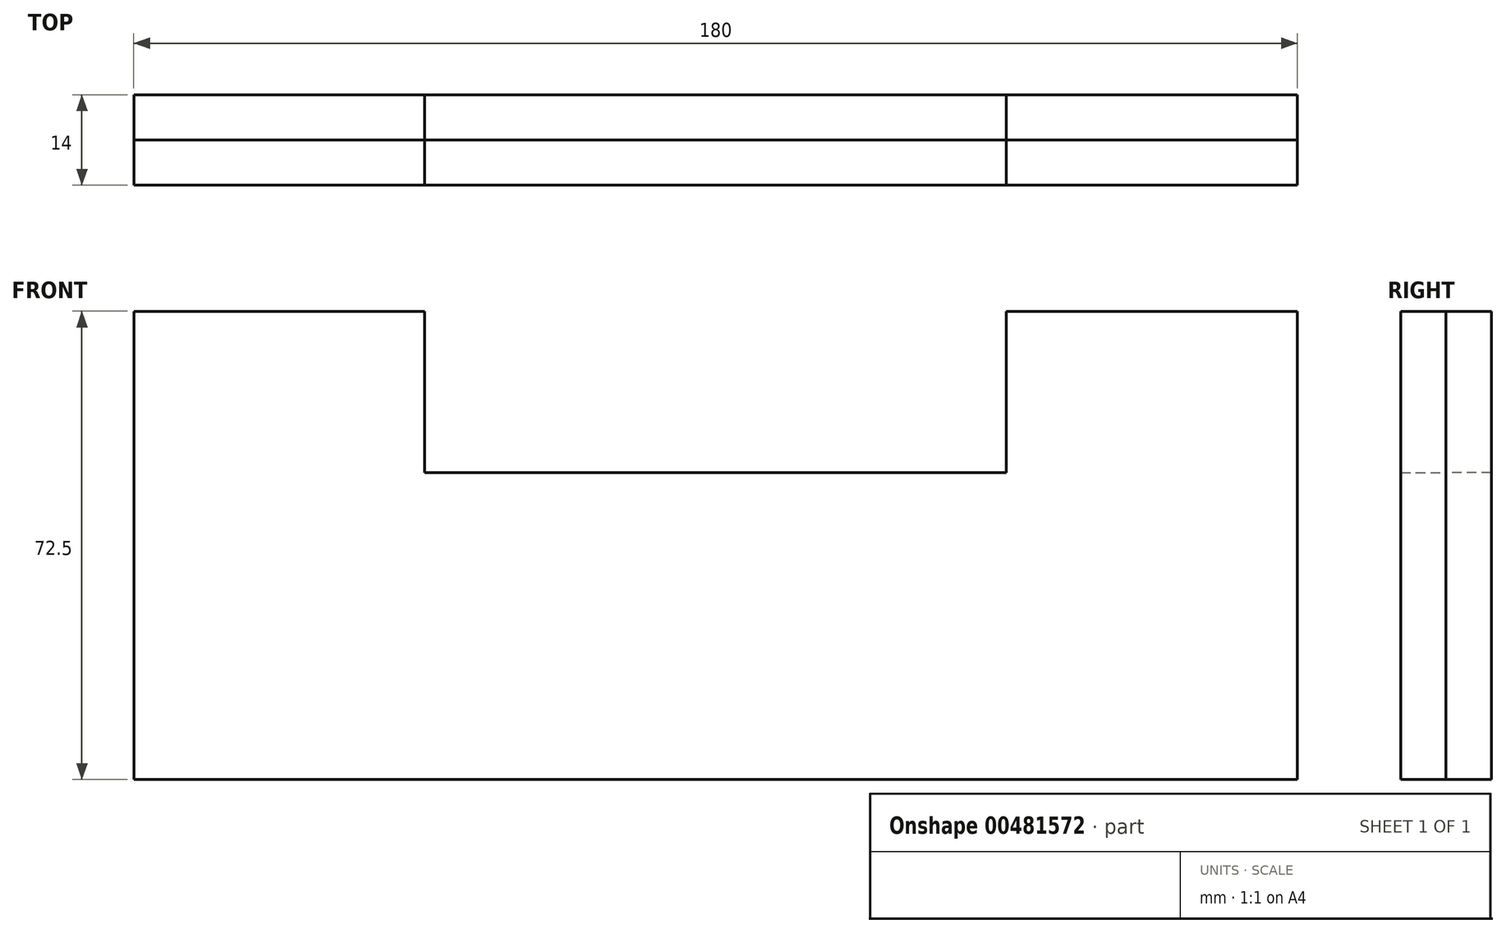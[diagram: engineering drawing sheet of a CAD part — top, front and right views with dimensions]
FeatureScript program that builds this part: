
annotation { "Feature Type Name" : "Feature", "Feature Type Description" : "" }
export const myFeature = defineFeature(function(context is Context, id is Id, definition is map)
    precondition{}
    {
        {
            var Q0;
            Q0=qCreatedBy(makeId("Front.planeOp"),FACE);
            var sketch = newSketch(context, id + "F0", { "sketchPlane" : qUnion([Q0])});
            skLineSegment(sketch, "E0", {"start": v(-72.22, 38.43) * mm, "end": v(-72.22, 23.75) * mm});
            skLineSegment(sketch, "E1", {"start": v(-72.22, 23.75) * mm, "end": v(107.78, 23.75) * mm});
            skLineSegment(sketch, "E2", {"start": v(107.78, 23.75) * mm, "end": v(107.78, 96.25) * mm});
            skLineSegment(sketch, "E3", {"start": v(107.78, 96.25) * mm, "end": v(62.78, 96.25) * mm});
            skLineSegment(sketch, "E4", {"start": v(62.78, 96.25) * mm, "end": v(62.78, 71.25) * mm});
            skLineSegment(sketch, "E5", {"start": v(62.78, 71.25) * mm, "end": v(-27.22, 71.25) * mm});
            skLineSegment(sketch, "E6", {"start": v(-27.22, 71.25) * mm, "end": v(-27.22, 96.25) * mm});
            skLineSegment(sketch, "E7", {"start": v(-27.22, 96.25) * mm, "end": v(-72.22, 96.25) * mm});
            skLineSegment(sketch, "E8", {"start": v(-72.22, 96.25) * mm, "end": v(-72.22, 38.43) * mm});
            skSolve(sketch);
        }
        {
            var Q0;
            Q0=makeQuery(id+"F0.imprint","IMPRINT",FACE,{"disambiguationData":[TD([[makeQuery(id+"F0.imprint","IMPRINT",EDGE,{"derivedFrom":sQuery(id+"F0.wireOp",EDGE,"E0")}),1.0]])]});
            extrude(context, id + "F1", {"entities" : qUnion([Q0]), "depth" : 7 * mm});
        }
        {
            var Q0;
            Q0=makeQuery(id+"F1.opExtrude","SWEPT_BODY",BODY,{"disambiguationData":[OSD([sQuery(id+"F0.wireOp",EDGE,"E0"),sQuery(id+"F0.wireOp",EDGE,"E1"),sQuery(id+"F0.wireOp",EDGE,"E2"),sQuery(id+"F0.wireOp",EDGE,"E3"),sQuery(id+"F0.wireOp",EDGE,"E4"),sQuery(id+"F0.wireOp",EDGE,"E5"),sQuery(id+"F0.wireOp",EDGE,"E6"),sQuery(id+"F0.wireOp",EDGE,"E7"),sQuery(id+"F0.wireOp",EDGE,"E8")])]});
            var Q1;
            Q1=qCreatedBy(makeId("Front.planeOp"),FACE);
            mirror(context, id + "F2", {"entities" : qUnion([Q0]), "mirrorPlane" : qUnion([Q1])});
        }
    });
